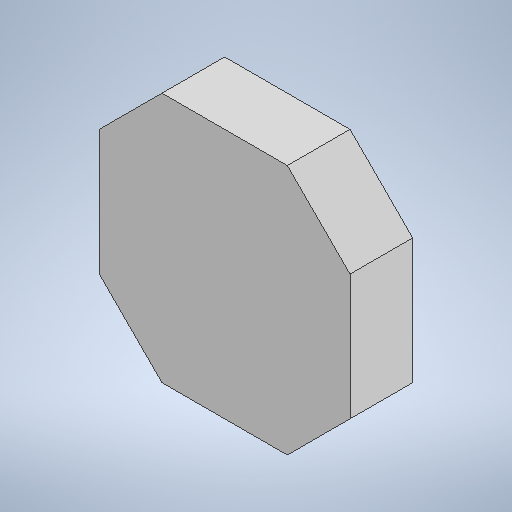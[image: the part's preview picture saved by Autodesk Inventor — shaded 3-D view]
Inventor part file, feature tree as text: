
AUTODESK INVENTOR PART (.ipt)
format: ipt  version: 2025.1 (Build 291241000, 241)  size: 212,480 bytes
history: native  units: mm
features: other x1, extrude x1, chamfer x1, sketch x1
ambient origin geometry x8: Origin, YZ Plane, XZ Plane, XY Plane, X Axis, Y Axis, Z Axis, Center Point
bodies: Body1 (feature_tree)
feature tree (4):
  other  "Sólido1"
  extrude  "Extrusión1"  Depth=20.0mm
  chamfer  "Chaflán1"  Distance=5.0mm
  sketch  "Boceto1"  dims[d0=20.0mm d1=20.0mm d2=5.0mm d3=0.0mm d4=5.0mm d5=2.0mm d6=45.0deg]
